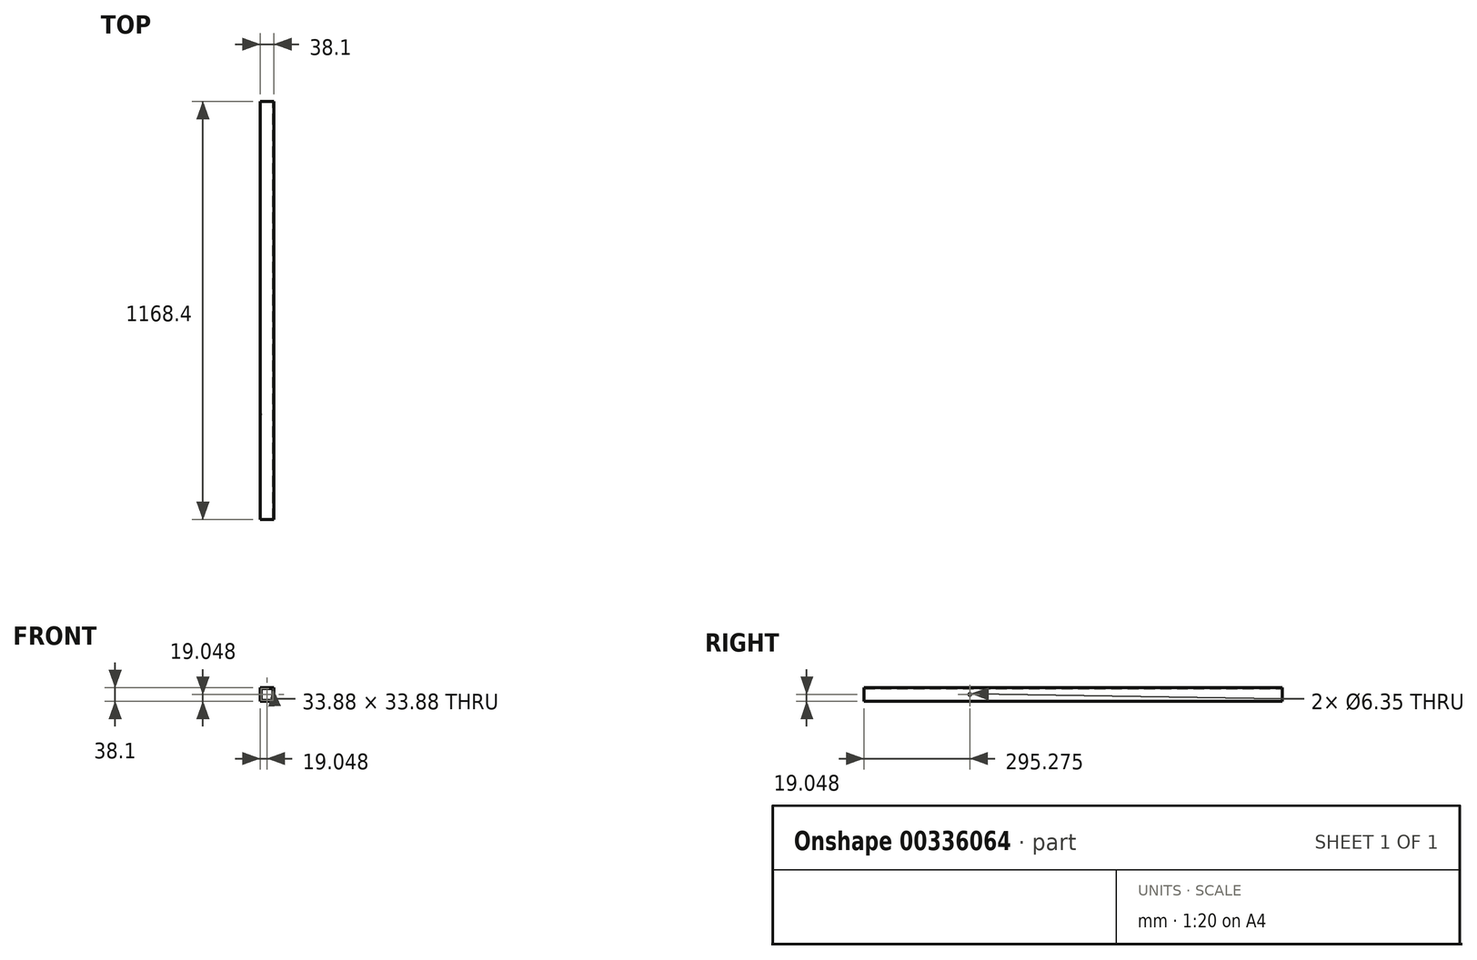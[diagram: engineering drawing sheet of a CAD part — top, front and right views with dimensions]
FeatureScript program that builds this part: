
annotation { "Feature Type Name" : "Feature", "Feature Type Description" : "" }
export const myFeature = defineFeature(function(context is Context, id is Id, definition is map)
    precondition{}
    {
        {
            var Q0;
            Q0=qCreatedBy(makeId("Front.planeOp"),FACE);
            var sketch = newSketch(context, id + "F0", { "sketchPlane" : qUnion([Q0])});
            skLineSegment(sketch, "E0.bottom", {"start": v(-54.03, 35.74) * mm, "end": v(-15.93, 35.74) * mm});
            skLineSegment(sketch, "E0.top", {"start": v(-54.03, -2.36) * mm, "end": v(-15.93, -2.36) * mm});
            skLineSegment(sketch, "E0.left", {"start": v(-54.03, 35.74) * mm, "end": v(-54.03, -2.36) * mm});
            skLineSegment(sketch, "E0.right", {"start": v(-15.93, 35.74) * mm, "end": v(-15.93, -2.36) * mm});
            skLineSegment(sketch, "E1.0", {"start": v(-18.04, 33.63) * mm, "end": v(-18.04, -0.25) * mm});
            skLineSegment(sketch, "E1.1", {"start": v(-51.92, 33.63) * mm, "end": v(-18.04, 33.63) * mm});
            skLineSegment(sketch, "E1.2", {"start": v(-51.92, 33.63) * mm, "end": v(-51.92, -0.25) * mm});
            skLineSegment(sketch, "E1.3", {"start": v(-51.92, -0.25) * mm, "end": v(-18.04, -0.25) * mm});
            skSolve(sketch);
        }
        {
            var Q0;
            Q0 = qSketchRegion(id + "F0", true);
            extrude(context, id + "F1", {"entities" : qUnion([Q0]), "depth" : 1168.4 * mm});
        }
        {
            var Q0;
            Q0=makeQuery(id+"F1.opExtrude","SWEPT_FACE",FACE,{"disambiguationData":[OSD([sQuery(id+"F0.wireOp",EDGE,"E0.left")])]});
            var sketch = newSketch(context, id + "F2", { "sketchPlane" : qUnion([Q0])});
            skPoint(sketch, "E2.centerSnap0", {"position": v(0, 16.69) * mm});
            skCircle(sketch, "E3", {"center": v(873.13, 16.69) * mm, "radius": 3.17 * mm});
            skPoint(sketch, "E3.centerSnap0", {"position": v(1168.4, 16.69) * mm});
            skSolve(sketch);
        }
        {
            var Q0;
            Q0 = qSketchRegion(id + "F2", true);
            extrude(context, id + "F3", {"entities" : qUnion([Q0]), "operationType" : NewBodyOperationType.REMOVE, "oppositeDirection" : true, "depth" : 76.2 * mm});
        }
    });
